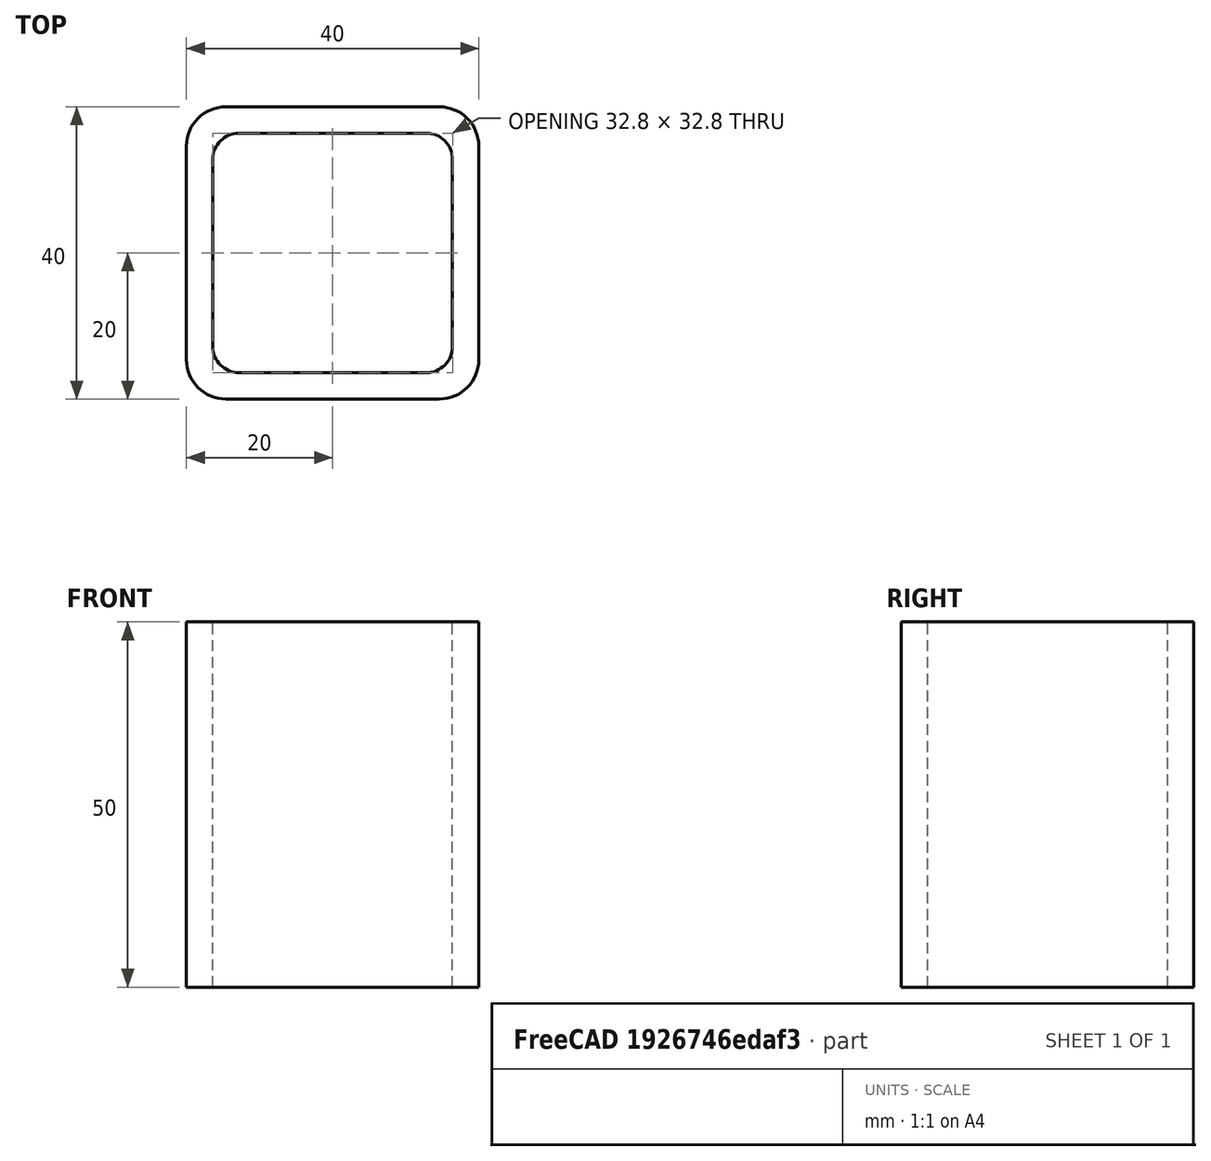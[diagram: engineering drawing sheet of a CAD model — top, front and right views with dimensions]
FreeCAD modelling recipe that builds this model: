
FCSTD DOCUMENT  (FreeCAD 0.15R4671 (Git))
Label: Square hollow section 40x40x3.6 EN10219 S235JRH
License: All rights reserved
LicenseURL: http://en.wikipedia.org/wiki/All_rights_reserved
objects: Sketcher::SketchObject×1, Part::Extrusion×1
note: 2 computed .brp shape members not serialized (recipe doc carries the construction recipe); baked Part::Feature solids carry a one-line shape summary decoded from their .brp

FEATURE [Sketcher::SketchObject] Sketch
  sketch-geometry (16):
    g0: LineSegment StartX=-12.8 StartY=16.4 StartZ=0 EndX=12.8 EndY=16.4 EndZ=0
    g1: LineSegment StartX=16.4 StartY=12.8 StartZ=0 EndX=16.4 EndY=-12.8 EndZ=0
    g2: LineSegment StartX=12.8 StartY=-16.4 StartZ=0 EndX=-12.8 EndY=-16.4 EndZ=0
    g3: LineSegment StartX=-16.4 StartY=-12.8 StartZ=0 EndX=-16.4 EndY=12.8 EndZ=0
    g4: LineSegment StartX=-14.6 StartY=20 StartZ=0 EndX=14.6 EndY=20 EndZ=0
    g5: LineSegment StartX=20 StartY=14.6 StartZ=0 EndX=20 EndY=-14.6 EndZ=0
    g6: LineSegment StartX=14.6 StartY=-20 StartZ=0 EndX=-14.6 EndY=-20 EndZ=0
    g7: LineSegment StartX=-20 StartY=-14.6 StartZ=0 EndX=-20 EndY=14.6 EndZ=0
    g8: ArcOfCircle CenterX=-12.8 CenterY=12.8 CenterZ=0 NormalX=0 NormalY=0 NormalZ=1 Radius=3.6 StartAngle=1.5708 EndAngle=3.14159
    g9: ArcOfCircle CenterX=12.8 CenterY=12.8 CenterZ=0 NormalX=0 NormalY=0 NormalZ=1 Radius=3.6 StartAngle=0 EndAngle=1.5708
    g10: ArcOfCircle CenterX=12.8 CenterY=-12.8 CenterZ=0 NormalX=0 NormalY=0 NormalZ=1 Radius=3.6 StartAngle=4.71239 EndAngle=6.28319
    g11: ArcOfCircle CenterX=-12.8 CenterY=-12.8 CenterZ=0 NormalX=0 NormalY=0 NormalZ=1 Radius=3.6 StartAngle=3.14159 EndAngle=4.71239
    g12: ArcOfCircle CenterX=14.6 CenterY=14.6 CenterZ=0 NormalX=0 NormalY=0 NormalZ=1 Radius=5.4 StartAngle=0 EndAngle=1.5708
    g13: ArcOfCircle CenterX=14.6 CenterY=-14.6 CenterZ=0 NormalX=0 NormalY=0 NormalZ=1 Radius=5.4 StartAngle=4.71239 EndAngle=6.28319
    g14: ArcOfCircle CenterX=-14.6 CenterY=-14.6 CenterZ=0 NormalX=0 NormalY=0 NormalZ=1 Radius=5.4 StartAngle=3.14159 EndAngle=4.71239
    g15: ArcOfCircle CenterX=-14.6 CenterY=14.6 CenterZ=0 NormalX=0 NormalY=0 NormalZ=1 Radius=5.4 StartAngle=1.5708 EndAngle=3.14159
  constraints (36):
    c: Horizontal(g2)
    c: Vertical(g3)
    c: Horizontal(g6)
    c: Vertical(g7)
    c: Tangent(g3,g8) = 1.5708
    c: Tangent(g0,g8) = 1.5708
    c: Tangent(g0,g9) = 1.5708
    c: Tangent(g1,g9) = 1.5708
    c: Tangent(g1,g10) = 1.5708
    c: Tangent(g2,g10) = 1.5708
    c: Tangent(g2,g11) = 1.5708
    c: Tangent(g3,g11) = 1.5708
    c: Tangent(g4,g12) = 1.5708
    c: Tangent(g5,g12) = 1.5708
    c: Tangent(g5,g13) = 1.5708
    c: Tangent(g6,g13) = 1.5708
    c: Tangent(g6,g14) = 1.5708
    c: Tangent(g7,g14) = 1.5708
    c: Tangent(g7,g15) = 1.5708
    c: Tangent(g4,g15) = 1.5708
    c: Equal(g9,g8)
    c: Equal(g9,g11)
    c: Equal(g9,g10)
    c: Equal(g12,g15)
    c: Equal(g12,g14)
    c: Equal(g12,g13)
    c: Symmetric(g4,g6,g-1)
    c: Symmetric(g7,g5,g-2)
    c: DistanceY(g4,g6) = -40
    c: DistanceX(g7,g5) = 40
    c: Symmetric(g3,g1,g-2)
    c: Symmetric(g0,g2,g-1)
    c: DistanceY(g0,g4) = 3.6
    c: DistanceX(g5,g1) = -3.6
    c: Radius(g9) = 3.6
    c: Radius(g12) = 5.4
FEATURE [Part::Extrusion] Extrude  label="Square hollow section 40x40x3.6 EN10219 S235JRH"
  Base = -> Sketch
  Dir = (0,0,50)
  Solid = true
